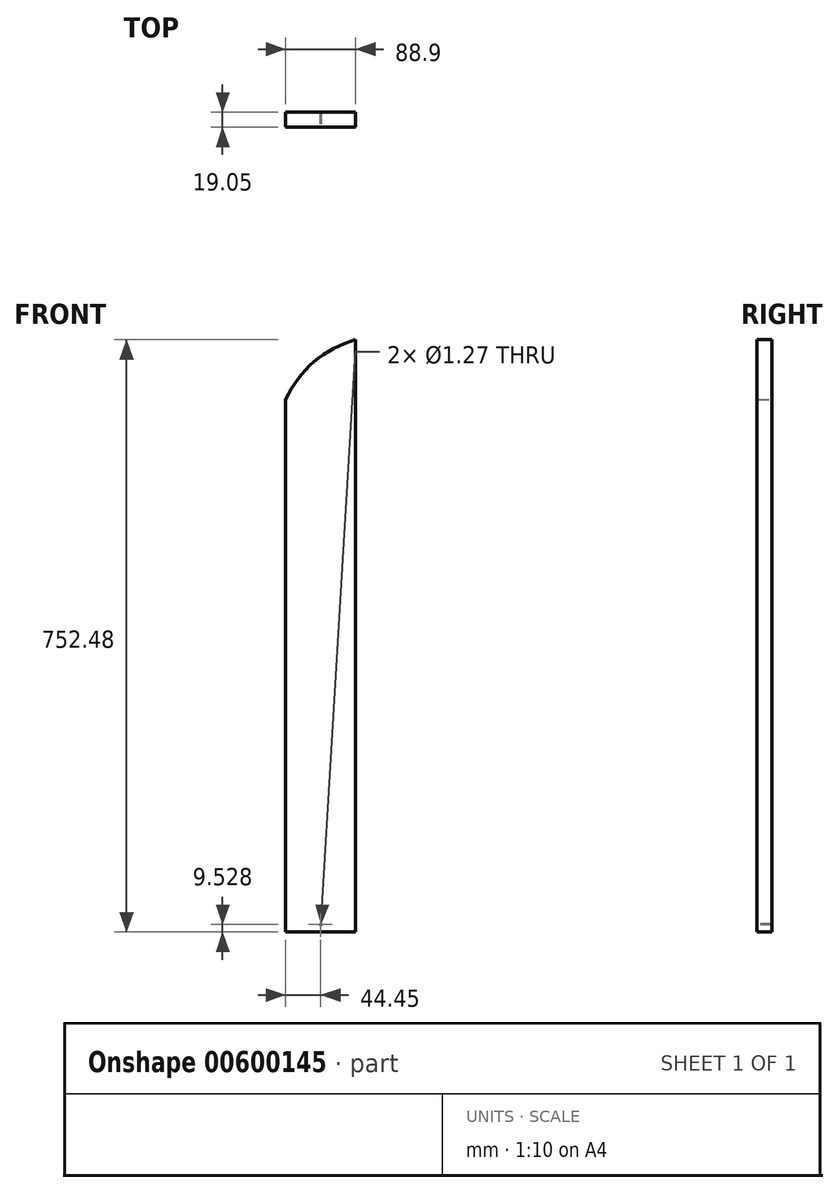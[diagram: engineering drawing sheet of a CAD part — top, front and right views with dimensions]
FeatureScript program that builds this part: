
annotation { "Feature Type Name" : "Feature", "Feature Type Description" : "" }
export const myFeature = defineFeature(function(context is Context, id is Id, definition is map)
    precondition{}
    {
        {
            var Q0;
            Q0=qCreatedBy(makeId("Front.planeOp"),FACE);
            var sketch = newSketch(context, id + "F0", { "sketchPlane" : qUnion([Q0])});
            skLineSegment(sketch, "E0.top", {"start": v(-44.45, -376.24) * mm, "end": v(44.45, -376.24) * mm});
            skLineSegment(sketch, "E0.left", {"start": v(-44.45, 300.04) * mm, "end": v(-44.45, -376.24) * mm});
            skLineSegment(sketch, "E0.right", {"start": v(44.45, 376.24) * mm, "end": v(44.45, -376.24) * mm});
            skLineSegment(sketch, "E1", {"start": v(44.45, 376.24) * mm, "end": v(-44.45, -376.24) * mm, "construction": true});
            skArc(sketch, "E2", {"start": v(44.45, 376.24) * mm, "mid": v(-8.62, 348.2) * mm, "end": v(-44.45, 300.04) * mm});
            skSolve(sketch);
        }
        {
            var Q0;
            Q0 = qSketchRegion(id + "F0", true);
            extrude(context, id + "F1", {"entities" : qUnion([Q0]), "depth" : 19.05 * mm, "offsetDistance" : 25.4 * mm});
        }
        {
            var Q0;
            Q0=makeQuery(id+"F1.opExtrude","CAP_FACE",FACE,{"disambiguationData":[OSD([sQuery(id+"F0.wireOp",EDGE,"E0.top"),sQuery(id+"F0.wireOp",EDGE,"E0.left"),sQuery(id+"F0.wireOp",EDGE,"E0.right"),sQuery(id+"F0.wireOp",EDGE,"E2")])],"isStart":false});
            var sketch = newSketch(context, id + "F2", { "sketchPlane" : qUnion([Q0])});
            skCircle(sketch, "E3", {"center": v(0, -366.71) * mm, "radius": 0.64 * mm});
            skSolve(sketch);
        }
        {
            var Q0;
            Q0 = qSketchRegion(id + "F2", true);
            extrude(context, id + "F3", {"entities" : qUnion([Q0]), "operationType" : NewBodyOperationType.REMOVE, "endBound" : BoundingType.THROUGH_ALL, "oppositeDirection" : true, "depth" : 25.4 * mm, "offsetDistance" : 25.4 * mm});
        }
    });
